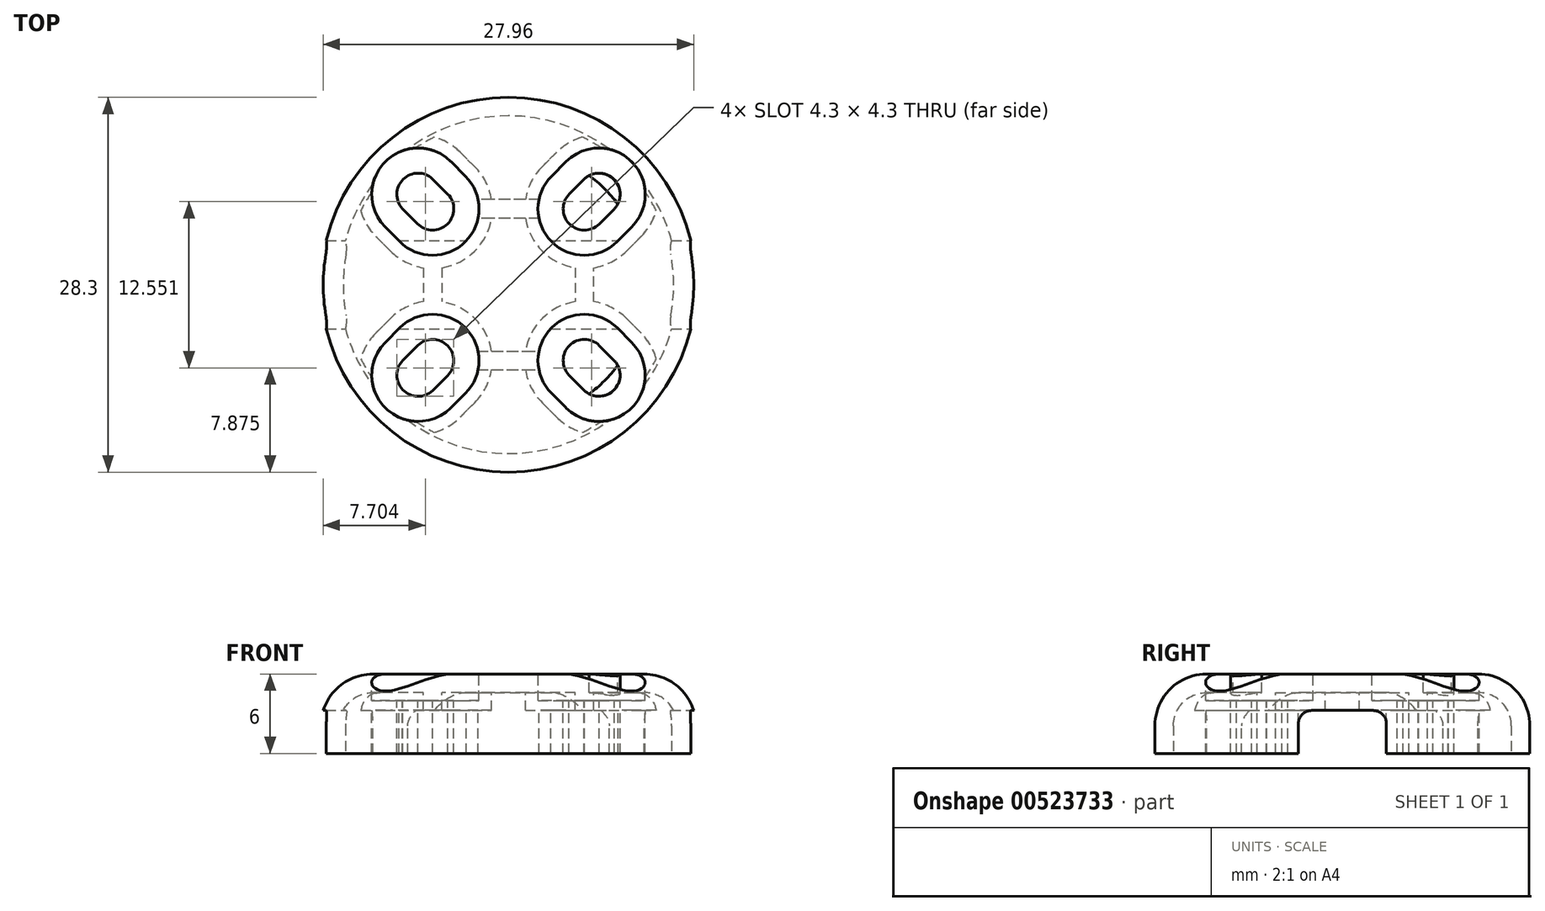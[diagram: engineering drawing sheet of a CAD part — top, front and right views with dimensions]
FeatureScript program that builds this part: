
annotation { "Feature Type Name" : "Feature", "Feature Type Description" : "" }
export const myFeature = defineFeature(function(context is Context, id is Id, definition is map)
    precondition{}
    {
        {
            var Q0;
            Q0=qCreatedBy(makeId("Right.planeOp"),FACE);
            var sketch = newSketch(context, id + "F0", { "sketchPlane" : qUnion([Q0])});
            skLineSegment(sketch, "E0", {"start": v(0, 4.6) * mm, "end": v(10.25, 4.6) * mm});
            skLineSegment(sketch, "E1", {"start": v(14.15, 0) * mm, "end": v(12.75, 0) * mm});
            skLineSegment(sketch, "E2", {"start": v(0, 4.6) * mm, "end": v(0, 6) * mm});
            skArc(sketch, "E3", {"start": v(18.65, 0) * mm, "mid": v(15.57, 7.42) * mm, "end": v(8.15, 10.5) * mm});
            skLineSegment(sketch, "E4", {"start": v(0, 10.5) * mm, "end": v(8.15, 10.5) * mm});
            skLineSegment(sketch, "E5", {"start": v(0, 10.5) * mm, "end": v(0, 6) * mm});
            skArc(sketch, "E6", {"start": v(12.75, 2.1) * mm, "mid": v(12.02, 3.87) * mm, "end": v(10.25, 4.6) * mm});
            skLineSegment(sketch, "E7", {"start": v(12.75, 0) * mm, "end": v(12.75, 2.1) * mm});
            skArc(sketch, "E8", {"start": v(14.15, 2.1) * mm, "mid": v(13, 4.86) * mm, "end": v(10.25, 6) * mm});
            skPoint(sketch, "E9.start.orphan", {"position": v(14.15, 0) * mm});
            skLineSegment(sketch, "E10", {"start": v(14.15, 0) * mm, "end": v(14.15, 2.1) * mm});
            skLineSegment(sketch, "E11", {"start": v(0, 6) * mm, "end": v(10.25, 6) * mm});
            skLineSegment(sketch, "E12", {"start": v(18.65, 0) * mm, "end": v(14.15, 0) * mm});
            skSolve(sketch);
        }
        {
            var Q0;
            Q0=makeQuery(id+"F0.imprint","IMPRINT",FACE,{"disambiguationData":[TD([[makeQuery(id+"F0.imprint","IMPRINT",EDGE,{"derivedFrom":sQuery(id+"F0.wireOp",EDGE,"h2fEWCMI-qm59-RIvp-Rzqm-nfMBG9C9NMks")}),-1.0]])]});
            var Q1;
            Q1=makeQuery(id+"F0.imprint","IMPRINT",FACE,{"disambiguationData":[TD([[makeQuery(id+"F0.imprint","IMPRINT",EDGE,{"derivedFrom":sQuery(id+"F0.wireOp",EDGE,"E0")}),1.0]])]});
            var Q2;
            Q2=sQuery(id+"F0.wireOp",EDGE,"E2");
            revolve(context, id + "F1", {"entities" : qUnion([Q0, Q1]), "axis" : qUnion([Q2]), "revolveType" : RevolveType.FULL});
        }
        {
            var Q0;
            Q0=makeQuery(id+"F1.opRevolve","SWEPT_FACE",FACE,{"disambiguationData":[OSD([sQuery(id+"F0.wireOp",EDGE,"E11")])]});
            var sketch = newSketch(context, id + "F2", { "sketchPlane" : qUnion([Q0])});
            skArc(sketch, "E13", {"start": v(-5.72, 7.98) * mm, "mid": v(-7.94, 7.97) * mm, "end": v(-8, 5.74) * mm});
            skArc(sketch, "E14", {"start": v(-6.86, 4.6) * mm, "mid": v(-4.6, 4.58) * mm, "end": v(-4.57, 6.83) * mm});
            skLineSegment(sketch, "E15", {"start": v(10.65, -10.65) * mm, "end": v(-11.04, 11.04) * mm, "construction": true});
            skLineSegment(sketch, "E16", {"start": v(-8, 5.74) * mm, "end": v(-6.86, 4.6) * mm});
            skLineSegment(sketch, "E17", {"start": v(-5.72, 7.98) * mm, "end": v(-4.57, 6.83) * mm});
            skArc(sketch, "E18.1.0", {"start": v(-7.98, -5.72) * mm, "mid": v(-7.97, -7.94) * mm, "end": v(-5.74, -8) * mm});
            skLineSegment(sketch, "E18.1.1", {"start": v(-5.74, -8) * mm, "end": v(-4.6, -6.86) * mm});
            skArc(sketch, "E18.1.2", {"start": v(-4.6, -6.86) * mm, "mid": v(-4.58, -4.6) * mm, "end": v(-6.83, -4.57) * mm});
            skLineSegment(sketch, "E18.1.3", {"start": v(-7.98, -5.72) * mm, "end": v(-6.83, -4.57) * mm});
            skArc(sketch, "E18.2.0", {"start": v(5.72, -7.98) * mm, "mid": v(7.94, -7.97) * mm, "end": v(8, -5.74) * mm});
            skLineSegment(sketch, "E18.2.1", {"start": v(8, -5.74) * mm, "end": v(6.86, -4.6) * mm});
            skArc(sketch, "E18.2.2", {"start": v(6.86, -4.6) * mm, "mid": v(4.6, -4.58) * mm, "end": v(4.57, -6.83) * mm});
            skLineSegment(sketch, "E18.2.3", {"start": v(5.72, -7.98) * mm, "end": v(4.57, -6.83) * mm});
            skArc(sketch, "E18.3.0", {"start": v(7.98, 5.72) * mm, "mid": v(7.97, 7.94) * mm, "end": v(5.74, 8) * mm});
            skLineSegment(sketch, "E18.3.1", {"start": v(5.74, 8) * mm, "end": v(4.6, 6.86) * mm});
            skArc(sketch, "E18.3.2", {"start": v(4.6, 6.86) * mm, "mid": v(4.58, 4.6) * mm, "end": v(6.83, 4.57) * mm});
            skLineSegment(sketch, "E18.3.3", {"start": v(7.98, 5.72) * mm, "end": v(6.83, 4.57) * mm});
            skPoint(sketch, "E18.center", {"position": v(0, 0) * mm});
            skArc(sketch, "E19", {"start": v(-4.35, 9.3) * mm, "mid": v(-9.3, 9.3) * mm, "end": v(-9.3, 4.35) * mm});
            skLineSegment(sketch, "E20", {"start": v(-9.3, 4.35) * mm, "end": v(-8.2, 3.25) * mm});
            skLineSegment(sketch, "E21", {"start": v(-4.35, 9.3) * mm, "end": v(-3.25, 8.2) * mm});
            skArc(sketch, "E22.trimOffspring", {"start": v(-8.2, 3.25) * mm, "mid": v(-3.25, 3.25) * mm, "end": v(-3.25, 8.2) * mm});
            skArc(sketch, "E23.1.0", {"start": v(-9.3, -4.35) * mm, "mid": v(-9.3, -9.3) * mm, "end": v(-4.35, -9.3) * mm});
            skLineSegment(sketch, "E23.1.1", {"start": v(-9.3, -4.35) * mm, "end": v(-8.2, -3.25) * mm});
            skArc(sketch, "E23.1.2", {"start": v(-3.25, -8.2) * mm, "mid": v(-3.25, -3.25) * mm, "end": v(-8.2, -3.25) * mm});
            skLineSegment(sketch, "E23.1.3", {"start": v(-4.35, -9.3) * mm, "end": v(-3.25, -8.2) * mm});
            skArc(sketch, "E23.2.0", {"start": v(4.35, -9.3) * mm, "mid": v(9.3, -9.3) * mm, "end": v(9.3, -4.35) * mm});
            skLineSegment(sketch, "E23.2.1", {"start": v(4.35, -9.3) * mm, "end": v(3.25, -8.2) * mm});
            skArc(sketch, "E23.2.2", {"start": v(8.2, -3.25) * mm, "mid": v(3.25, -3.25) * mm, "end": v(3.25, -8.2) * mm});
            skLineSegment(sketch, "E23.2.3", {"start": v(9.3, -4.35) * mm, "end": v(8.2, -3.25) * mm});
            skArc(sketch, "E23.3.0", {"start": v(9.3, 4.35) * mm, "mid": v(9.3, 9.3) * mm, "end": v(4.35, 9.3) * mm});
            skLineSegment(sketch, "E23.3.1", {"start": v(9.3, 4.35) * mm, "end": v(8.2, 3.25) * mm});
            skArc(sketch, "E23.3.2", {"start": v(3.25, 8.2) * mm, "mid": v(3.25, 3.25) * mm, "end": v(8.2, 3.25) * mm});
            skLineSegment(sketch, "E23.3.3", {"start": v(4.35, 9.3) * mm, "end": v(3.25, 8.2) * mm});
            skArc(sketch, "E24", {"start": v(-3.64, 10) * mm, "mid": v(-10, 10) * mm, "end": v(-10, 3.64) * mm});
            skArc(sketch, "E25", {"start": v(-8.9, 2.55) * mm, "mid": v(-2.55, 2.55) * mm, "end": v(-2.55, 8.9) * mm});
            skLineSegment(sketch, "E26", {"start": v(-10, 3.64) * mm, "end": v(-8.9, 2.55) * mm});
            skLineSegment(sketch, "E27", {"start": v(-3.64, 10) * mm, "end": v(-2.55, 8.9) * mm});
            skArc(sketch, "E28.1.0", {"start": v(-10, -3.64) * mm, "mid": v(-10, -10) * mm, "end": v(-3.64, -10) * mm});
            skArc(sketch, "E28.1.1", {"start": v(-2.55, -8.9) * mm, "mid": v(-2.55, -2.55) * mm, "end": v(-8.9, -2.55) * mm});
            skLineSegment(sketch, "E28.1.2", {"start": v(-10, -3.64) * mm, "end": v(-8.9, -2.55) * mm});
            skLineSegment(sketch, "E28.1.3", {"start": v(-3.64, -10) * mm, "end": v(-2.55, -8.9) * mm});
            skArc(sketch, "E28.2.0", {"start": v(3.64, -10) * mm, "mid": v(10, -10) * mm, "end": v(10, -3.64) * mm});
            skArc(sketch, "E28.2.1", {"start": v(8.9, -2.55) * mm, "mid": v(2.55, -2.55) * mm, "end": v(2.55, -8.9) * mm});
            skLineSegment(sketch, "E28.2.2", {"start": v(3.64, -10) * mm, "end": v(2.55, -8.9) * mm});
            skLineSegment(sketch, "E28.2.3", {"start": v(10, -3.64) * mm, "end": v(8.9, -2.55) * mm});
            skArc(sketch, "E28.3.0", {"start": v(10, 3.64) * mm, "mid": v(10, 10) * mm, "end": v(3.64, 10) * mm});
            skArc(sketch, "E28.3.1", {"start": v(2.55, 8.9) * mm, "mid": v(2.55, 2.55) * mm, "end": v(8.9, 2.55) * mm});
            skLineSegment(sketch, "E28.3.2", {"start": v(10, 3.64) * mm, "end": v(8.9, 2.55) * mm});
            skLineSegment(sketch, "E28.3.3", {"start": v(3.64, 10) * mm, "end": v(2.55, 8.9) * mm});
            skSolve(sketch);
        }
        {
            var Q0;
            {var subQ2=sQuery(id+"F2.wireOp",EDGE,"E23.2.0");Q0=makeQuery(id+"F2.imprint","IMPRINT",FACE,{"disambiguationData":[TD([[makeQuery(id+"F2.imprint","IMPRINT",EDGE,{"derivedFrom":subQ2}),-1.0]])]});}
            var Q1;
            {var subQ1=sQuery(id+"F2.wireOp",EDGE,"E23.2.2");Q1=makeQuery(id+"F2.imprint","IMPRINT",FACE,{"disambiguationData":[TD([[makeQuery(id+"F2.imprint","IMPRINT",EDGE,{"derivedFrom":subQ1}),-1.0]])]});}
            var Q2;
            {var subQ2=sQuery(id+"F2.wireOp",EDGE,"E23.1.0");Q2=makeQuery(id+"F2.imprint","IMPRINT",FACE,{"disambiguationData":[TD([[makeQuery(id+"F2.imprint","IMPRINT",EDGE,{"derivedFrom":subQ2}),-1.0]])]});}
            var Q3;
            {var subQ1=sQuery(id+"F2.wireOp",EDGE,"E23.1.2");Q3=makeQuery(id+"F2.imprint","IMPRINT",FACE,{"disambiguationData":[TD([[makeQuery(id+"F2.imprint","IMPRINT",EDGE,{"derivedFrom":subQ1}),-1.0]])]});}
            var Q4;
            {var subQ1=sQuery(id+"F2.wireOp",EDGE,"E22.trimOffspring");Q4=makeQuery(id+"F2.imprint","IMPRINT",FACE,{"disambiguationData":[TD([[makeQuery(id+"F2.imprint","IMPRINT",EDGE,{"derivedFrom":subQ1}),-1.0]])]});}
            var Q5;
            {var subQ2=sQuery(id+"F2.wireOp",EDGE,"E19");Q5=makeQuery(id+"F2.imprint","IMPRINT",FACE,{"disambiguationData":[TD([[makeQuery(id+"F2.imprint","IMPRINT",EDGE,{"derivedFrom":subQ2}),-1.0]])]});}
            var Q6;
            {var subQ1=sQuery(id+"F2.wireOp",EDGE,"E23.3.2");Q6=makeQuery(id+"F2.imprint","IMPRINT",FACE,{"disambiguationData":[TD([[makeQuery(id+"F2.imprint","IMPRINT",EDGE,{"derivedFrom":subQ1}),-1.0]])]});}
            var Q7;
            {var subQ2=sQuery(id+"F2.wireOp",EDGE,"E23.3.0");Q7=makeQuery(id+"F2.imprint","IMPRINT",FACE,{"disambiguationData":[TD([[makeQuery(id+"F2.imprint","IMPRINT",EDGE,{"derivedFrom":subQ2}),-1.0]])]});}
            extrude(context, id + "F3", {"entities" : qUnion([Q0, Q1, Q2, Q3, Q4, Q5, Q6, Q7]), "operationType" : NewBodyOperationType.ADD, "oppositeDirection" : true, "depth" : 2.75 * mm, "offsetDistance" : 25 * mm});
        }
        {
            var Q0;
            {var subQ1=sQuery(id+"F2.wireOp",EDGE,"E23.3.0");Q0=makeQuery(id+"F2.imprint","IMPRINT",FACE,{"disambiguationData":[TD([[makeQuery(id+"F2.imprint","IMPRINT",EDGE,{"derivedFrom":subQ1}),1.0]])]});}
            var Q1;
            {var subQ4=sQuery(id+"F2.wireOp",EDGE,"E18.3.1");Q1=makeQuery(id+"F2.imprint","IMPRINT",FACE,{"disambiguationData":[TD([[makeQuery(id+"F2.imprint","IMPRINT",EDGE,{"derivedFrom":subQ4}),-1.0]])]});}
            var Q2;
            {var subQ0=sQuery(id+"F2.wireOp",EDGE,"E18.3.1");Q2=makeQuery(id+"F2.imprint","IMPRINT",FACE,{"disambiguationData":[TD([[makeQuery(id+"F2.imprint","IMPRINT",EDGE,{"derivedFrom":subQ0}),1.0]])]});}
            var Q3;
            {var subQ0=sQuery(id+"F2.wireOp",EDGE,"E18.3.0");var subQ1=makeQuery(id+"F1.opRevolve","SWEPT_EDGE",EDGE,{"disambiguationData":[OSD([sQuery(id+"F0.wireOp",EDGE,"E8"),sQuery(id+"F0.wireOp",EDGE,"E11")])]});var subQ2=makeQuery(id+"F2.imprint","INTERSECT",VERTEX,{"disambiguationData":[OD(0.0)],"derivedFrom":[subQ1,subQ0]});Q3=makeQuery(id+"F2.imprint","IMPRINT",FACE,{"disambiguationData":[TD([[makeQuery(id+"F2.imprint","IMPRINT",EDGE,{"disambiguationData":[TD([[subQ2,-1.0]])],"derivedFrom":subQ0}),1.0]])]});}
            var Q4;
            {var subQ4=sQuery(id+"F2.wireOp",EDGE,"E18.2.1");Q4=makeQuery(id+"F2.imprint","IMPRINT",FACE,{"disambiguationData":[TD([[makeQuery(id+"F2.imprint","IMPRINT",EDGE,{"derivedFrom":subQ4}),-1.0]])]});}
            var Q5;
            {var subQ1=sQuery(id+"F2.wireOp",EDGE,"E23.2.0");Q5=makeQuery(id+"F2.imprint","IMPRINT",FACE,{"disambiguationData":[TD([[makeQuery(id+"F2.imprint","IMPRINT",EDGE,{"derivedFrom":subQ1}),1.0]])]});}
            var Q6;
            {var subQ0=sQuery(id+"F2.wireOp",EDGE,"E18.2.0");var subQ1=makeQuery(id+"F1.opRevolve","SWEPT_EDGE",EDGE,{"disambiguationData":[OSD([sQuery(id+"F0.wireOp",EDGE,"E8"),sQuery(id+"F0.wireOp",EDGE,"E11")])]});var subQ2=makeQuery(id+"F2.imprint","INTERSECT",VERTEX,{"disambiguationData":[OD(0.0)],"derivedFrom":[subQ1,subQ0]});Q6=makeQuery(id+"F2.imprint","IMPRINT",FACE,{"disambiguationData":[TD([[makeQuery(id+"F2.imprint","IMPRINT",EDGE,{"disambiguationData":[TD([[subQ2,-1.0]])],"derivedFrom":subQ0}),1.0]])]});}
            var Q7;
            {var subQ1=sQuery(id+"F2.wireOp",EDGE,"E23.1.0");Q7=makeQuery(id+"F2.imprint","IMPRINT",FACE,{"disambiguationData":[TD([[makeQuery(id+"F2.imprint","IMPRINT",EDGE,{"derivedFrom":subQ1}),1.0]])]});}
            var Q8;
            {var subQ4=sQuery(id+"F2.wireOp",EDGE,"E18.1.1");Q8=makeQuery(id+"F2.imprint","IMPRINT",FACE,{"disambiguationData":[TD([[makeQuery(id+"F2.imprint","IMPRINT",EDGE,{"derivedFrom":subQ4}),-1.0]])]});}
            var Q9;
            {var subQ4=sQuery(id+"F2.wireOp",EDGE,"E18.1.1");Q9=makeQuery(id+"F2.imprint","IMPRINT",FACE,{"disambiguationData":[TD([[makeQuery(id+"F2.imprint","IMPRINT",EDGE,{"derivedFrom":subQ4}),1.0]])]});}
            var Q10;
            {var subQ0=sQuery(id+"F2.wireOp",EDGE,"E18.1.0");var subQ1=makeQuery(id+"F1.opRevolve","SWEPT_EDGE",EDGE,{"disambiguationData":[OSD([sQuery(id+"F0.wireOp",EDGE,"E8"),sQuery(id+"F0.wireOp",EDGE,"E11")])]});var subQ2=makeQuery(id+"F2.imprint","INTERSECT",VERTEX,{"disambiguationData":[OD(0.0)],"derivedFrom":[subQ1,subQ0]});Q10=makeQuery(id+"F2.imprint","IMPRINT",FACE,{"disambiguationData":[TD([[makeQuery(id+"F2.imprint","IMPRINT",EDGE,{"disambiguationData":[TD([[subQ2,-1.0]])],"derivedFrom":subQ0}),1.0]])]});}
            var Q11;
            {var subQ1=sQuery(id+"F2.wireOp",EDGE,"E19");Q11=makeQuery(id+"F2.imprint","IMPRINT",FACE,{"disambiguationData":[TD([[makeQuery(id+"F2.imprint","IMPRINT",EDGE,{"derivedFrom":subQ1}),1.0]])]});}
            var Q12;
            Q12=makeQuery(id+"F2.imprint","IMPRINT",FACE,{"disambiguationData":[TD([[makeQuery(id+"F2.imprint","IMPRINT",EDGE,{"derivedFrom":sQuery(id+"F2.wireOp",EDGE,"E14")}),-1.0]])]});
            var Q13;
            Q13=makeQuery(id+"F2.imprint","IMPRINT",FACE,{"disambiguationData":[TD([[makeQuery(id+"F2.imprint","IMPRINT",EDGE,{"derivedFrom":sQuery(id+"F2.wireOp",EDGE,"E14")}),1.0]])]});
            var Q14;
            {var subQ0=sQuery(id+"F2.wireOp",EDGE,"E13");var subQ1=makeQuery(id+"F1.opRevolve","SWEPT_EDGE",EDGE,{"disambiguationData":[OSD([sQuery(id+"F0.wireOp",EDGE,"E8"),sQuery(id+"F0.wireOp",EDGE,"E11")])]});var subQ2=makeQuery(id+"F2.imprint","INTERSECT",VERTEX,{"disambiguationData":[OD(0.0)],"derivedFrom":[subQ1,subQ0]});Q14=makeQuery(id+"F2.imprint","IMPRINT",FACE,{"disambiguationData":[TD([[makeQuery(id+"F2.imprint","IMPRINT",EDGE,{"disambiguationData":[TD([[subQ2,-1.0]])],"derivedFrom":subQ0}),1.0]])]});}
            var Q15;
            {var subQ0=sQuery(id+"F2.wireOp",EDGE,"E18.2.1");Q15=makeQuery(id+"F2.imprint","IMPRINT",FACE,{"disambiguationData":[TD([[makeQuery(id+"F2.imprint","IMPRINT",EDGE,{"derivedFrom":subQ0}),1.0]])]});}
            extrude(context, id + "F4", {"entities" : qUnion([Q0, Q1, Q2, Q3, Q4, Q5, Q6, Q7, Q8, Q9, Q10, Q11, Q12, Q13, Q14, Q15]), "operationType" : NewBodyOperationType.ADD, "oppositeDirection" : true, "depth" : 6 * mm, "offsetDistance" : 25 * mm});
        }
        {
            var Q0;
            Q0=makeQuery(id+"F2.imprint","IMPRINT",FACE,{"disambiguationData":[TD([[makeQuery(id+"F2.imprint","IMPRINT",EDGE,{"derivedFrom":sQuery(id+"F2.wireOp",EDGE,"E18.3.0")}),-1.0]])]});
            var Q1;
            {var subQ0=sQuery(id+"F2.wireOp",EDGE,"E18.3.2");var subQ1=makeQuery(id+"F1.opRevolve","SWEPT_EDGE",EDGE,{"disambiguationData":[OSD([sQuery(id+"F0.wireOp",EDGE,"h2fEWCMI-qm59-RIvp-Rzqm-nfMBG9C9NMks"),sQuery(id+"F0.wireOp",EDGE,"E9")])]});var subQ2=makeQuery(id+"F2.imprint","INTERSECT",VERTEX,{"disambiguationData":[OD(0.0)],"derivedFrom":[subQ1,subQ0]});Q1=makeQuery(id+"F2.imprint","IMPRINT",FACE,{"disambiguationData":[TD([[makeQuery(id+"F2.imprint","IMPRINT",EDGE,{"disambiguationData":[TD([[subQ2,-1.0]])],"derivedFrom":subQ0}),-1.0]])]});}
            var Q2;
            {var subQ0=sQuery(id+"F2.wireOp",EDGE,"E14");var subQ1=makeQuery(id+"F1.opRevolve","SWEPT_EDGE",EDGE,{"disambiguationData":[OSD([sQuery(id+"F0.wireOp",EDGE,"h2fEWCMI-qm59-RIvp-Rzqm-nfMBG9C9NMks"),sQuery(id+"F0.wireOp",EDGE,"E9")])]});var subQ2=makeQuery(id+"F2.imprint","INTERSECT",VERTEX,{"disambiguationData":[OD(0.0)],"derivedFrom":[subQ1,subQ0]});Q2=makeQuery(id+"F2.imprint","IMPRINT",FACE,{"disambiguationData":[TD([[makeQuery(id+"F2.imprint","IMPRINT",EDGE,{"disambiguationData":[TD([[subQ2,-1.0]])],"derivedFrom":subQ0}),-1.0]])]});}
            var Q3;
            Q3=makeQuery(id+"F2.imprint","IMPRINT",FACE,{"disambiguationData":[TD([[makeQuery(id+"F2.imprint","IMPRINT",EDGE,{"derivedFrom":sQuery(id+"F2.wireOp",EDGE,"E13")}),-1.0]])]});
            var Q4;
            {var subQ0=sQuery(id+"F2.wireOp",EDGE,"E18.1.2");var subQ1=makeQuery(id+"F1.opRevolve","SWEPT_EDGE",EDGE,{"disambiguationData":[OSD([sQuery(id+"F0.wireOp",EDGE,"h2fEWCMI-qm59-RIvp-Rzqm-nfMBG9C9NMks"),sQuery(id+"F0.wireOp",EDGE,"E9")])]});var subQ2=makeQuery(id+"F2.imprint","INTERSECT",VERTEX,{"disambiguationData":[OD(0.0)],"derivedFrom":[subQ1,subQ0]});Q4=makeQuery(id+"F2.imprint","IMPRINT",FACE,{"disambiguationData":[TD([[makeQuery(id+"F2.imprint","IMPRINT",EDGE,{"disambiguationData":[TD([[subQ2,-1.0]])],"derivedFrom":subQ0}),-1.0]])]});}
            var Q5;
            {var subQ0=sQuery(id+"F2.wireOp",EDGE,"E18.2.2");var subQ1=makeQuery(id+"F1.opRevolve","SWEPT_EDGE",EDGE,{"disambiguationData":[OSD([sQuery(id+"F0.wireOp",EDGE,"h2fEWCMI-qm59-RIvp-Rzqm-nfMBG9C9NMks"),sQuery(id+"F0.wireOp",EDGE,"E9")])]});var subQ2=makeQuery(id+"F2.imprint","INTERSECT",VERTEX,{"disambiguationData":[OD(0.0)],"derivedFrom":[subQ1,subQ0]});Q5=makeQuery(id+"F2.imprint","IMPRINT",FACE,{"disambiguationData":[TD([[makeQuery(id+"F2.imprint","IMPRINT",EDGE,{"disambiguationData":[TD([[subQ2,-1.0]])],"derivedFrom":subQ0}),-1.0]])]});}
            var Q6;
            Q6=makeQuery(id+"F2.imprint","IMPRINT",FACE,{"disambiguationData":[TD([[makeQuery(id+"F2.imprint","IMPRINT",EDGE,{"derivedFrom":sQuery(id+"F2.wireOp",EDGE,"E18.2.0")}),-1.0]])]});
            var Q7;
            Q7=makeQuery(id+"F2.imprint","IMPRINT",FACE,{"disambiguationData":[TD([[makeQuery(id+"F2.imprint","IMPRINT",EDGE,{"derivedFrom":sQuery(id+"F2.wireOp",EDGE,"E18.1.0")}),-1.0]])]});
            var Q8;
            {var subQ1=sQuery(id+"F2.wireOp",EDGE,"E23.3.0");Q8=makeQuery(id+"F2.imprint","IMPRINT",FACE,{"disambiguationData":[TD([[makeQuery(id+"F2.imprint","IMPRINT",EDGE,{"derivedFrom":subQ1}),1.0]])]});}
            var Q9;
            {var subQ1=sQuery(id+"F2.wireOp",EDGE,"E23.2.0");Q9=makeQuery(id+"F2.imprint","IMPRINT",FACE,{"disambiguationData":[TD([[makeQuery(id+"F2.imprint","IMPRINT",EDGE,{"derivedFrom":subQ1}),1.0]])]});}
            var Q10;
            {var subQ1=sQuery(id+"F2.wireOp",EDGE,"E19");Q10=makeQuery(id+"F2.imprint","IMPRINT",FACE,{"disambiguationData":[TD([[makeQuery(id+"F2.imprint","IMPRINT",EDGE,{"derivedFrom":subQ1}),1.0]])]});}
            var Q11;
            {var subQ1=sQuery(id+"F2.wireOp",EDGE,"E23.1.0");Q11=makeQuery(id+"F2.imprint","IMPRINT",FACE,{"disambiguationData":[TD([[makeQuery(id+"F2.imprint","IMPRINT",EDGE,{"derivedFrom":subQ1}),1.0]])]});}
            extrude(context, id + "F5", {"entities" : qUnion([Q0, Q1, Q2, Q3, Q4, Q5, Q6, Q7, Q8, Q9, Q10, Q11]), "operationType" : NewBodyOperationType.REMOVE, "oppositeDirection" : true, "depth" : 2 * mm, "offsetDistance" : 25 * mm});
        }
        {
            var Q0;
            Q0=makeQuery(id+"F2.imprint","IMPRINT",FACE,{"disambiguationData":[TD([[makeQuery(id+"F2.imprint","IMPRINT",EDGE,{"derivedFrom":sQuery(id+"F2.wireOp",EDGE,"E18.3.0")}),1.0]])]});
            var Q1;
            {var subQ0=sQuery(id+"F2.wireOp",EDGE,"E18.3.2");var subQ1=makeQuery(id+"F1.opRevolve","SWEPT_EDGE",EDGE,{"disambiguationData":[OSD([sQuery(id+"F0.wireOp",EDGE,"h2fEWCMI-qm59-RIvp-Rzqm-nfMBG9C9NMks"),sQuery(id+"F0.wireOp",EDGE,"E9")])]});var subQ2=makeQuery(id+"F2.imprint","INTERSECT",VERTEX,{"disambiguationData":[OD(0.0)],"derivedFrom":[subQ1,subQ0]});Q1=makeQuery(id+"F2.imprint","IMPRINT",FACE,{"disambiguationData":[TD([[makeQuery(id+"F2.imprint","IMPRINT",EDGE,{"disambiguationData":[TD([[subQ2,-1.0]])],"derivedFrom":subQ0}),1.0]])]});}
            var Q2;
            {var subQ0=sQuery(id+"F2.wireOp",EDGE,"E14");var subQ1=makeQuery(id+"F1.opRevolve","SWEPT_EDGE",EDGE,{"disambiguationData":[OSD([sQuery(id+"F0.wireOp",EDGE,"h2fEWCMI-qm59-RIvp-Rzqm-nfMBG9C9NMks"),sQuery(id+"F0.wireOp",EDGE,"E9")])]});var subQ2=makeQuery(id+"F2.imprint","INTERSECT",VERTEX,{"disambiguationData":[OD(0.0)],"derivedFrom":[subQ1,subQ0]});Q2=makeQuery(id+"F2.imprint","IMPRINT",FACE,{"disambiguationData":[TD([[makeQuery(id+"F2.imprint","IMPRINT",EDGE,{"disambiguationData":[TD([[subQ2,-1.0]])],"derivedFrom":subQ0}),1.0]])]});}
            var Q3;
            Q3=makeQuery(id+"F2.imprint","IMPRINT",FACE,{"disambiguationData":[TD([[makeQuery(id+"F2.imprint","IMPRINT",EDGE,{"derivedFrom":sQuery(id+"F2.wireOp",EDGE,"E13")}),1.0]])]});
            var Q4;
            {var subQ0=sQuery(id+"F2.wireOp",EDGE,"E18.2.2");var subQ1=makeQuery(id+"F1.opRevolve","SWEPT_EDGE",EDGE,{"disambiguationData":[OSD([sQuery(id+"F0.wireOp",EDGE,"h2fEWCMI-qm59-RIvp-Rzqm-nfMBG9C9NMks"),sQuery(id+"F0.wireOp",EDGE,"E9")])]});var subQ2=makeQuery(id+"F2.imprint","INTERSECT",VERTEX,{"disambiguationData":[OD(0.0)],"derivedFrom":[subQ1,subQ0]});Q4=makeQuery(id+"F2.imprint","IMPRINT",FACE,{"disambiguationData":[TD([[makeQuery(id+"F2.imprint","IMPRINT",EDGE,{"disambiguationData":[TD([[subQ2,-1.0]])],"derivedFrom":subQ0}),1.0]])]});}
            var Q5;
            Q5=makeQuery(id+"F2.imprint","IMPRINT",FACE,{"disambiguationData":[TD([[makeQuery(id+"F2.imprint","IMPRINT",EDGE,{"derivedFrom":sQuery(id+"F2.wireOp",EDGE,"E18.2.0")}),1.0]])]});
            var Q6;
            {var subQ0=sQuery(id+"F2.wireOp",EDGE,"E18.1.2");var subQ1=makeQuery(id+"F1.opRevolve","SWEPT_EDGE",EDGE,{"disambiguationData":[OSD([sQuery(id+"F0.wireOp",EDGE,"h2fEWCMI-qm59-RIvp-Rzqm-nfMBG9C9NMks"),sQuery(id+"F0.wireOp",EDGE,"E9")])]});var subQ2=makeQuery(id+"F2.imprint","INTERSECT",VERTEX,{"disambiguationData":[OD(0.0)],"derivedFrom":[subQ1,subQ0]});Q6=makeQuery(id+"F2.imprint","IMPRINT",FACE,{"disambiguationData":[TD([[makeQuery(id+"F2.imprint","IMPRINT",EDGE,{"disambiguationData":[TD([[subQ2,-1.0]])],"derivedFrom":subQ0}),1.0]])]});}
            var Q7;
            Q7=makeQuery(id+"F2.imprint","IMPRINT",FACE,{"disambiguationData":[TD([[makeQuery(id+"F2.imprint","IMPRINT",EDGE,{"derivedFrom":sQuery(id+"F2.wireOp",EDGE,"E18.1.0")}),1.0]])]});
            var Q8;
            {var subQ0=sQuery(id+"F2.wireOp",EDGE,"E18.3.0");var subQ1=makeQuery(id+"F1.opRevolve","SWEPT_EDGE",EDGE,{"disambiguationData":[OSD([sQuery(id+"F0.wireOp",EDGE,"E8"),sQuery(id+"F0.wireOp",EDGE,"E11")])]});var subQ2=makeQuery(id+"F2.imprint","INTERSECT",VERTEX,{"disambiguationData":[OD(0.0)],"derivedFrom":[subQ1,subQ0]});Q8=makeQuery(id+"F2.imprint","IMPRINT",FACE,{"disambiguationData":[TD([[makeQuery(id+"F2.imprint","IMPRINT",EDGE,{"disambiguationData":[TD([[subQ2,-1.0]])],"derivedFrom":subQ0}),1.0]])]});}
            var Q9;
            {var subQ0=sQuery(id+"F2.wireOp",EDGE,"E13");var subQ1=makeQuery(id+"F1.opRevolve","SWEPT_EDGE",EDGE,{"disambiguationData":[OSD([sQuery(id+"F0.wireOp",EDGE,"E8"),sQuery(id+"F0.wireOp",EDGE,"E11")])]});var subQ2=makeQuery(id+"F2.imprint","INTERSECT",VERTEX,{"disambiguationData":[OD(0.0)],"derivedFrom":[subQ1,subQ0]});Q9=makeQuery(id+"F2.imprint","IMPRINT",FACE,{"disambiguationData":[TD([[makeQuery(id+"F2.imprint","IMPRINT",EDGE,{"disambiguationData":[TD([[subQ2,-1.0]])],"derivedFrom":subQ0}),1.0]])]});}
            var Q10;
            {var subQ0=sQuery(id+"F2.wireOp",EDGE,"E18.1.0");var subQ1=makeQuery(id+"F1.opRevolve","SWEPT_EDGE",EDGE,{"disambiguationData":[OSD([sQuery(id+"F0.wireOp",EDGE,"E8"),sQuery(id+"F0.wireOp",EDGE,"E11")])]});var subQ2=makeQuery(id+"F2.imprint","INTERSECT",VERTEX,{"disambiguationData":[OD(0.0)],"derivedFrom":[subQ1,subQ0]});Q10=makeQuery(id+"F2.imprint","IMPRINT",FACE,{"disambiguationData":[TD([[makeQuery(id+"F2.imprint","IMPRINT",EDGE,{"disambiguationData":[TD([[subQ2,-1.0]])],"derivedFrom":subQ0}),1.0]])]});}
            var Q11;
            {var subQ0=sQuery(id+"F2.wireOp",EDGE,"E18.2.0");var subQ1=makeQuery(id+"F1.opRevolve","SWEPT_EDGE",EDGE,{"disambiguationData":[OSD([sQuery(id+"F0.wireOp",EDGE,"E8"),sQuery(id+"F0.wireOp",EDGE,"E11")])]});var subQ2=makeQuery(id+"F2.imprint","INTERSECT",VERTEX,{"disambiguationData":[OD(0.0)],"derivedFrom":[subQ1,subQ0]});Q11=makeQuery(id+"F2.imprint","IMPRINT",FACE,{"disambiguationData":[TD([[makeQuery(id+"F2.imprint","IMPRINT",EDGE,{"disambiguationData":[TD([[subQ2,-1.0]])],"derivedFrom":subQ0}),1.0]])]});}
            extrude(context, id + "F6", {"entities" : qUnion([Q0, Q1, Q2, Q3, Q4, Q5, Q6, Q7, Q8, Q9, Q10, Q11]), "operationType" : NewBodyOperationType.REMOVE, "oppositeDirection" : true, "depth" : 25 * mm, "offsetDistance" : 25 * mm});
        }
        {
            var Q0;
            Q0=makeQuery(id+"F0.imprint","IMPRINT",FACE,{"disambiguationData":[TD([[makeQuery(id+"F0.imprint","IMPRINT",EDGE,{"derivedFrom":sQuery(id+"F0.wireOp",EDGE,"E3")}),1.0]])]});
            var Q1;
            Q1=sQuery(id+"F0.wireOp",EDGE,"E5");
            revolve(context, id + "F7", {"operationType" : NewBodyOperationType.REMOVE, "entities" : qUnion([Q0]), "axis" : qUnion([Q1]), "revolveType" : RevolveType.FULL, "oppositeDirection" : true});
        }
        {
            var Q0;
            Q0=makeQuery(id+"F3.boolean.opBoolean","SPLIT",FACE,{"disambiguationData":[TD([makeQuery(id+"F3.opExtrude","SWEPT_FACE",FACE,{"disambiguationData":[OSD([sQuery(id+"F2.wireOp",EDGE,"E25")])]})])],"derivedFrom":makeQuery(id+"F1.opRevolve","SWEPT_FACE",FACE,{"disambiguationData":[OSD([sQuery(id+"F0.wireOp",EDGE,"E0")])]})});
            var sketch = newSketch(context, id + "F8", { "sketchPlane" : qUnion([Q0])});
            skLineSegment(sketch, "E29.bottom", {"start": v(-2.3, 6.43) * mm, "end": v(2.3, 6.43) * mm});
            skLineSegment(sketch, "E29.top", {"start": v(-2.3, 5.03) * mm, "end": v(2.3, 5.03) * mm});
            skArc(sketch, "E30.0", {"start": v(-2.55, 8.9) * mm, "mid": v(-2.55, 2.55) * mm, "end": v(-8.9, 2.55) * mm});
            skPoint(sketch, "E31.center", {"position": v(0, 0) * mm});
            skArc(sketch, "E32", {"start": v(-2.3, 5.03) * mm, "mid": v(-2.23, 5.73) * mm, "end": v(-2.3, 6.43) * mm});
            skArc(sketch, "E33", {"start": v(2.3, 6.43) * mm, "mid": v(2.23, 5.73) * mm, "end": v(2.3, 5.03) * mm});
            skArc(sketch, "E34.1.0", {"start": v(-5.03, -2.3) * mm, "mid": v(-5.73, -2.23) * mm, "end": v(-6.43, -2.3) * mm});
            skLineSegment(sketch, "E34.1.1", {"start": v(-6.43, -2.3) * mm, "end": v(-6.43, 2.3) * mm});
            skLineSegment(sketch, "E34.1.2", {"start": v(-5.03, -2.3) * mm, "end": v(-5.03, 2.3) * mm});
            skArc(sketch, "E34.1.3", {"start": v(-6.43, 2.3) * mm, "mid": v(-5.73, 2.23) * mm, "end": v(-5.03, 2.3) * mm});
            skArc(sketch, "E34.2.0", {"start": v(2.3, -5.03) * mm, "mid": v(2.23, -5.73) * mm, "end": v(2.3, -6.43) * mm});
            skLineSegment(sketch, "E34.2.1", {"start": v(2.3, -6.43) * mm, "end": v(-2.3, -6.43) * mm});
            skLineSegment(sketch, "E34.2.2", {"start": v(2.3, -5.03) * mm, "end": v(-2.3, -5.03) * mm});
            skArc(sketch, "E34.2.3", {"start": v(-2.3, -6.43) * mm, "mid": v(-2.23, -5.73) * mm, "end": v(-2.3, -5.03) * mm});
            skArc(sketch, "E34.3.0", {"start": v(5.03, 2.3) * mm, "mid": v(5.73, 2.23) * mm, "end": v(6.43, 2.3) * mm});
            skLineSegment(sketch, "E34.3.1", {"start": v(6.43, 2.3) * mm, "end": v(6.43, -2.3) * mm});
            skLineSegment(sketch, "E34.3.2", {"start": v(5.03, 2.3) * mm, "end": v(5.03, -2.3) * mm});
            skArc(sketch, "E34.3.3", {"start": v(6.43, -2.3) * mm, "mid": v(5.73, -2.23) * mm, "end": v(5.03, -2.3) * mm});
            skSolve(sketch);
        }
        {
            var Q0;
            Q0 = qSketchRegion(id + "F8", true);
            extrude(context, id + "F9", {"entities" : qUnion([Q0]), "operationType" : NewBodyOperationType.ADD, "depth" : 4.6 * mm, "offsetDistance" : 25 * mm});
        }
        {
            var Q0;
            Q0=qCreatedBy(makeId("Right.planeOp"),FACE);
            var sketch = newSketch(context, id + "F10", { "sketchPlane" : qUnion([Q0])});
            skLineSegment(sketch, "E35.bottom", {"start": v(3.33, 0) * mm, "end": v(-3.32, 0) * mm});
            skLineSegment(sketch, "E35.top", {"start": v(3.33, 3.25) * mm, "end": v(-3.33, 3.25) * mm});
            skLineSegment(sketch, "E35.left", {"start": v(3.33, 0) * mm, "end": v(3.33, 3.25) * mm});
            skLineSegment(sketch, "E35.right", {"start": v(-3.32, 0) * mm, "end": v(-3.33, 3.25) * mm});
            skSolve(sketch);
        }
        {
            var Q0;
            Q0 = qSketchRegion(id + "F10", true);
            extrude(context, id + "F11", {"entities" : qUnion([Q0]), "operationType" : NewBodyOperationType.REMOVE, "endBound" : BoundingType.SYMMETRIC, "oppositeDirection" : true, "depth" : 50 * mm, "offsetDistance" : 25 * mm});
        }
        {
            var Q0;
            {var subQ0=sQuery(id+"F10.wireOp",EDGE,"E35.top");var subQ1=sQuery(id+"F10.wireOp",EDGE,"E35.left");Q0=makeQuery(id+"F11.boolean.opBoolean","COPY",EDGE,{"disambiguationData":[topologyDisambiguationEdgeConnected([makeQuery(id+"F11.opExtrude","SWEPT_FACE",FACE,{"disambiguationData":[OSD([subQ0])]}),makeQuery(id+"F11.opExtrude","SWEPT_FACE",FACE,{"disambiguationData":[OSD([subQ1])]})]),OD(1.0)],"derivedFrom":makeQuery(id+"F11.opExtrude","SWEPT_EDGE",EDGE,{"disambiguationData":[OSD([subQ0,subQ1])]})});}
            var Q1;
            {var subQ0=sQuery(id+"F10.wireOp",EDGE,"E35.top");var subQ1=sQuery(id+"F10.wireOp",EDGE,"E35.right");Q1=makeQuery(id+"F11.boolean.opBoolean","COPY",EDGE,{"disambiguationData":[topologyDisambiguationEdgeConnected([makeQuery(id+"F11.opExtrude","SWEPT_FACE",FACE,{"disambiguationData":[OSD([subQ0])]}),makeQuery(id+"F11.opExtrude","SWEPT_FACE",FACE,{"disambiguationData":[OSD([subQ1])]})]),OD(1.0)],"derivedFrom":makeQuery(id+"F11.opExtrude","SWEPT_EDGE",EDGE,{"disambiguationData":[OSD([subQ0,subQ1])]})});}
            var Q2;
            {var subQ0=sQuery(id+"F10.wireOp",EDGE,"E35.top");var subQ1=sQuery(id+"F10.wireOp",EDGE,"E35.right");Q2=makeQuery(id+"F11.boolean.opBoolean","COPY",EDGE,{"disambiguationData":[topologyDisambiguationEdgeConnected([makeQuery(id+"F11.opExtrude","SWEPT_FACE",FACE,{"disambiguationData":[OSD([subQ0])]}),makeQuery(id+"F11.opExtrude","SWEPT_FACE",FACE,{"disambiguationData":[OSD([subQ1])]})]),OD(0.0)],"derivedFrom":makeQuery(id+"F11.opExtrude","SWEPT_EDGE",EDGE,{"disambiguationData":[OSD([subQ0,subQ1])]})});}
            var Q3;
            {var subQ0=sQuery(id+"F10.wireOp",EDGE,"E35.top");var subQ1=sQuery(id+"F10.wireOp",EDGE,"E35.left");Q3=makeQuery(id+"F11.boolean.opBoolean","COPY",EDGE,{"disambiguationData":[topologyDisambiguationEdgeConnected([makeQuery(id+"F11.opExtrude","SWEPT_FACE",FACE,{"disambiguationData":[OSD([subQ0])]}),makeQuery(id+"F11.opExtrude","SWEPT_FACE",FACE,{"disambiguationData":[OSD([subQ1])]})]),OD(0.0)],"derivedFrom":makeQuery(id+"F11.opExtrude","SWEPT_EDGE",EDGE,{"disambiguationData":[OSD([subQ0,subQ1])]})});}
            fillet(context, id + "F12", {"entities" : qUnion([Q0, Q1, Q2, Q3]), "radius" : 1 * mm, "tangentPropagation" : true, "allowEdgeOverflow" : false});
        }
    });
